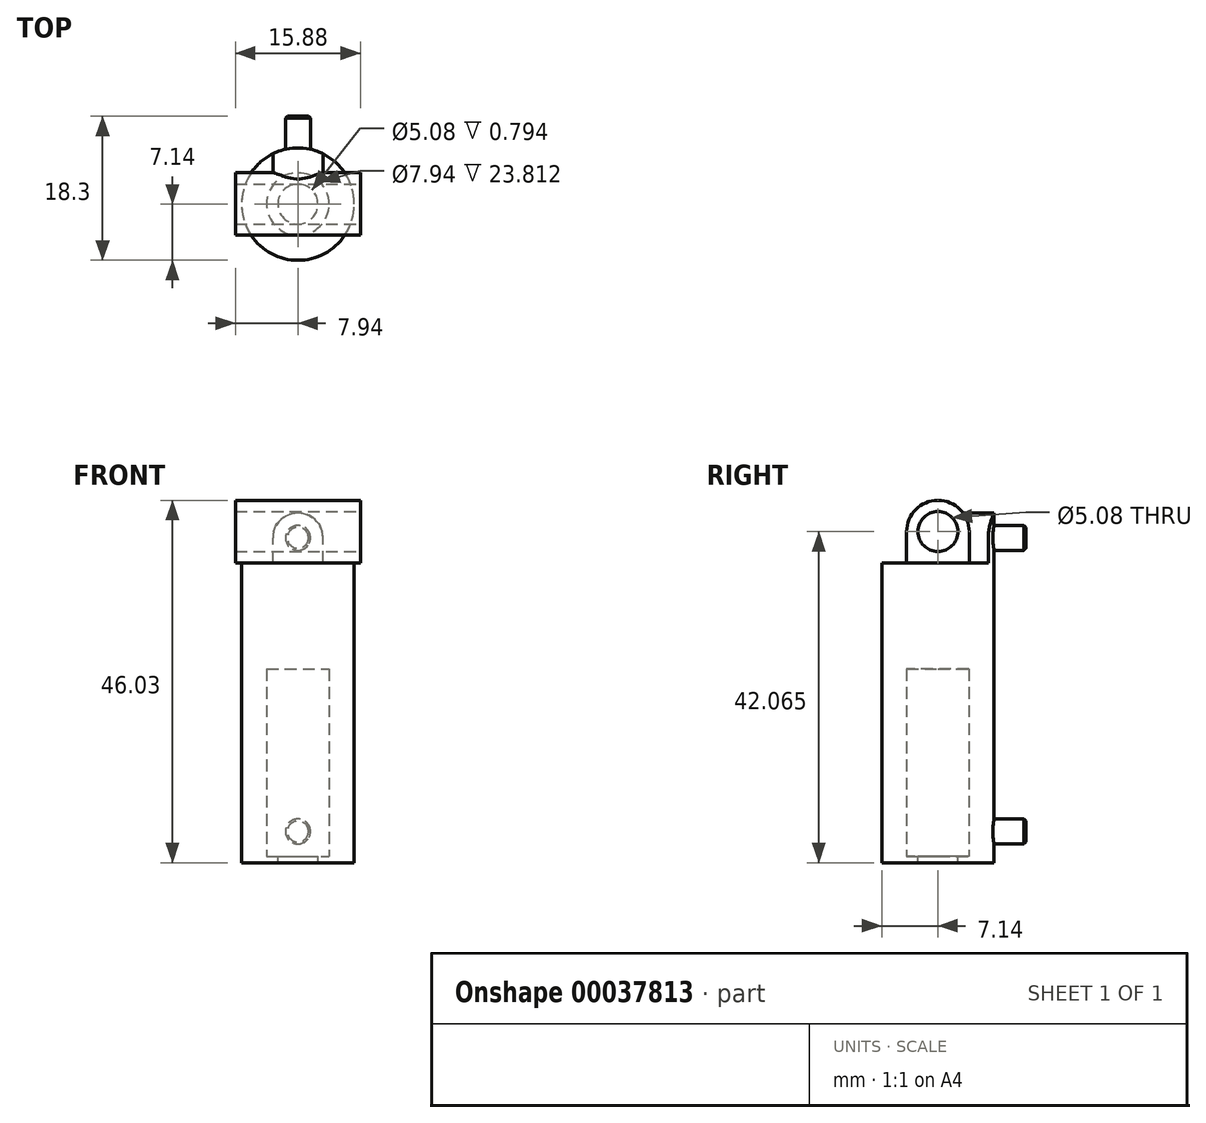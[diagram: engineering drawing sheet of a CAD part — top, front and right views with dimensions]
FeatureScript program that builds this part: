
annotation { "Feature Type Name" : "Feature", "Feature Type Description" : "" }
export const myFeature = defineFeature(function(context is Context, id is Id, definition is map)
    precondition{}
    {
        {
            var Q0;
            Q0=qCreatedBy(makeId("Top.planeOp"),FACE);
            var sketch = newSketch(context, id + "F0", { "sketchPlane" : qUnion([Q0])});
            skCircle(sketch, "E0", {"center": v(0, 0) * mm, "radius": 7.14 * mm});
            skSolve(sketch);
        }
        {
            var Q0;
            Q0=qSketchRegion(id+"F0",true);
            extrude(context, id + "F1", {"entities" : qUnion([Q0]), "depth" : 37.3 * mm});
        }
        {
            var Q0;
            Q0=makeQuery(id+"F1.opExtrude","CAP_FACE",FACE,{"disambiguationData":[OSD([sQuery(id+"F0.wireOp",EDGE,"E0")])],"isStart":false});
            var sketch = newSketch(context, id + "F2", { "sketchPlane" : qUnion([Q0])});
            skLineSegment(sketch, "E1.rect.bottom", {"start": v(7.94, 3.97) * mm, "end": v(-7.94, 3.97) * mm});
            skLineSegment(sketch, "E1.rect.top", {"start": v(7.94, -3.97) * mm, "end": v(-7.94, -3.97) * mm});
            skLineSegment(sketch, "E1.rect.left", {"start": v(7.94, 3.97) * mm, "end": v(7.94, -3.97) * mm});
            skLineSegment(sketch, "E1.rect.right", {"start": v(-7.94, 3.97) * mm, "end": v(-7.94, -3.97) * mm});
            skPoint(sketch, "E1.rect.middle", {"position": v(0, 0) * mm});
            skSolve(sketch);
        }
        {
            var Q0;
            Q0=qSketchRegion(id+"F2",true);
            extrude(context, id + "F3", {"entities" : qUnion([Q0]), "operationType" : NewBodyOperationType.ADD, "depth" : 7.94 * mm});
        }
        {
            var Q0;
            Q0=makeQuery(id+"F3.opExtrude","CAP_EDGE",EDGE,{"disambiguationData":[OSD([sQuery(id+"F2.wireOp",EDGE,"E1.rect.bottom")])],"isStart":false});
            var Q1;
            Q1=makeQuery(id+"F3.opExtrude","CAP_EDGE",EDGE,{"disambiguationData":[OSD([sQuery(id+"F2.wireOp",EDGE,"E1.rect.top")])],"isStart":false});
            fillet(context, id + "F4", {"entities" : qUnion([Q0, Q1]), "radius" : 3.97 * mm, "tangentPropagation" : true, "allowEdgeOverflow" : false});
        }
        {
            var Q0;
            Q0=makeQuery(id+"F3.opExtrude","SWEPT_FACE",FACE,{"disambiguationData":[OSD([sQuery(id+"F2.wireOp",EDGE,"E1.rect.left")])]});
            var sketch = newSketch(context, id + "F5", { "sketchPlane" : qUnion([Q0])});
            skCircle(sketch, "E2", {"center": v(0, 41.28) * mm, "radius": 2.54 * mm});
            skSolve(sketch);
        }
        {
            var Q0;
            Q0=qSketchRegion(id+"F5",true);
            var Q1;
            Q1=makeQuery(id+"F3.opExtrude","SWEPT_FACE",FACE,{"disambiguationData":[OSD([sQuery(id+"F2.wireOp",EDGE,"E1.rect.right")])]});
            extrude(context, id + "F6", {"entities" : qUnion([Q0]), "operationType" : NewBodyOperationType.REMOVE, "endBound" : BoundingType.UP_TO_SURFACE, "oppositeDirection" : true, "endBoundEntityFace" : qUnion([Q1]), "depth" : 25.4 * mm});
        }
        {
            var Q0;
            Q0=makeQuery(id+"F3.opExtrude","SWEPT_FACE",FACE,{"disambiguationData":[OSD([sQuery(id+"F2.wireOp",EDGE,"E1.rect.bottom")])]});
            var sketch = newSketch(context, id + "F7", { "sketchPlane" : qUnion([Q0])});
            skLineSegment(sketch, "E3.bottom", {"start": v(-3.18, 37.3) * mm, "end": v(3.17, 37.3) * mm});
            skLineSegment(sketch, "E3.top", {"start": v(-3.18, 40.48) * mm, "end": v(3.17, 40.48) * mm});
            skLineSegment(sketch, "E3.left", {"start": v(-3.18, 37.3) * mm, "end": v(-3.18, 40.48) * mm});
            skLineSegment(sketch, "E3.right", {"start": v(3.17, 37.3) * mm, "end": v(3.17, 40.48) * mm});
            skPoint(sketch, "E4", {"position": v(0, 37.3) * mm});
            skArc(sketch, "E5", {"start": v(3.17, 40.48) * mm, "mid": v(0, 43.66) * mm, "end": v(-3.18, 40.48) * mm});
            skSolve(sketch);
        }
        {
            var Q0;
            Q0=qSketchRegion(id+"F7",true);
            var Q1;
            Q1=makeQuery(id+"F1.opExtrude","SWEPT_FACE",FACE,{"disambiguationData":[OSD([sQuery(id+"F0.wireOp",EDGE,"E0")])]});
            var Q2;
            Q2=makeQuery(id+"F4.opFillet","BLEND_FACE",FACE,{"disambiguationData":[OSD([sQuery(id+"F2.wireOp",EDGE,"E1.rect.bottom")])]});
            extrude(context, id + "F8", {"entities" : qUnion([Q0]), "operationType" : NewBodyOperationType.ADD, "endBound" : BoundingType.UP_TO_SURFACE, "endBoundEntityFace" : qUnion([Q1]), "depth" : 25.4 * mm, "hasSecondDirection" : true, "secondDirectionBound" : SecondDirectionBoundingType.UP_TO_SURFACE, "secondDirectionOppositeDirection" : true, "secondDirectionBoundEntityFace" : qUnion([Q2]), "secondDirectionDepth" : 25.4 * mm});
        }
        {
            var Q0;
            Q0=qCreatedBy(makeId("Front.planeOp"),FACE);
            cPlane(context, id + "F9", {"entities" : qUnion([Q0]), "cplaneType" : CPlaneType.OFFSET, "offset" : 6.4 * mm, "oppositeDirection" : true, "width" : 152.4 * mm, "height" : 152.4 * mm});
        }
        {
            var Q0;
            Q0=qCreatedBy(id+"F9.planeOp",FACE);
            var sketch = newSketch(context, id + "F10", { "sketchPlane" : qUnion([Q0])});
            skCircle(sketch, "E6", {"center": v(0, 40.48) * mm, "radius": 1.59 * mm});
            skLineSegment(sketch, "E7", {"start": v(0, 40.48) * mm, "end": v(0, 3.18) * mm, "construction": true});
            skLineSegment(sketch, "E8", {"start": v(0, 3.18) * mm, "end": v(0, 0) * mm, "construction": true});
            skCircle(sketch, "E9", {"center": v(0, 3.18) * mm, "radius": 1.59 * mm});
            skSolve(sketch);
        }
        {
            var Q0;
            Q0=qSketchRegion(id+"F10",true);
            extrude(context, id + "F11", {"entities" : qUnion([Q0]), "operationType" : NewBodyOperationType.ADD, "oppositeDirection" : true, "depth" : 4.76 * mm});
        }
        {
            var Q0;
            Q0=makeQuery(id+"F11.opExtrude","CAP_EDGE",EDGE,{"disambiguationData":[OSD([sQuery(id+"F10.wireOp",EDGE,"E6")])],"isStart":false});
            var Q1;
            Q1=makeQuery(id+"F11.opExtrude","CAP_EDGE",EDGE,{"disambiguationData":[OSD([sQuery(id+"F10.wireOp",EDGE,"E9")])],"isStart":false});
            chamfer(context, id + "F12", {"entities" : qUnion([Q0, Q1]), "width" : 0.25 * mm, "tangentPropagation" : true});
        }
        {
            var Q0;
            Q0=makeQuery(id+"F1.opExtrude","CAP_FACE",FACE,{"disambiguationData":[OSD([sQuery(id+"F0.wireOp",EDGE,"E0")])],"isStart":true});
            var sketch = newSketch(context, id + "F13", { "sketchPlane" : qUnion([Q0])});
            skCircle(sketch, "E10", {"center": v(0, 0) * mm, "radius": 3.97 * mm});
            skSolve(sketch);
        }
        {
            var Q0;
            Q0 = qSketchRegion(id + "F13", true);
            extrude(context, id + "F14", {"entities" : qUnion([Q0]), "operationType" : NewBodyOperationType.REMOVE, "oppositeDirection" : true, "depth" : 23.8 * mm});
        }
        {
            var Q0;
            Q0=makeQuery(id+"F1.opExtrude","CAP_FACE",FACE,{"disambiguationData":[OSD([sQuery(id+"F0.wireOp",EDGE,"E0")])],"isStart":true});
            var sketch = newSketch(context, id + "F15", { "sketchPlane" : qUnion([Q0])});
            skCircle(sketch, "E11", {"center": v(0, 0) * mm, "radius": 2.54 * mm});
            skCircle(sketch, "E12", {"center": v(0, 0) * mm, "radius": 7.14 * mm});
            skSolve(sketch);
        }
        {
            var Q0;
            Q0 = qSketchRegion(id + "F15", true);
            extrude(context, id + "F16", {"entities" : qUnion([Q0]), "operationType" : NewBodyOperationType.ADD, "depth" : 0.8 * mm});
        }
    });
